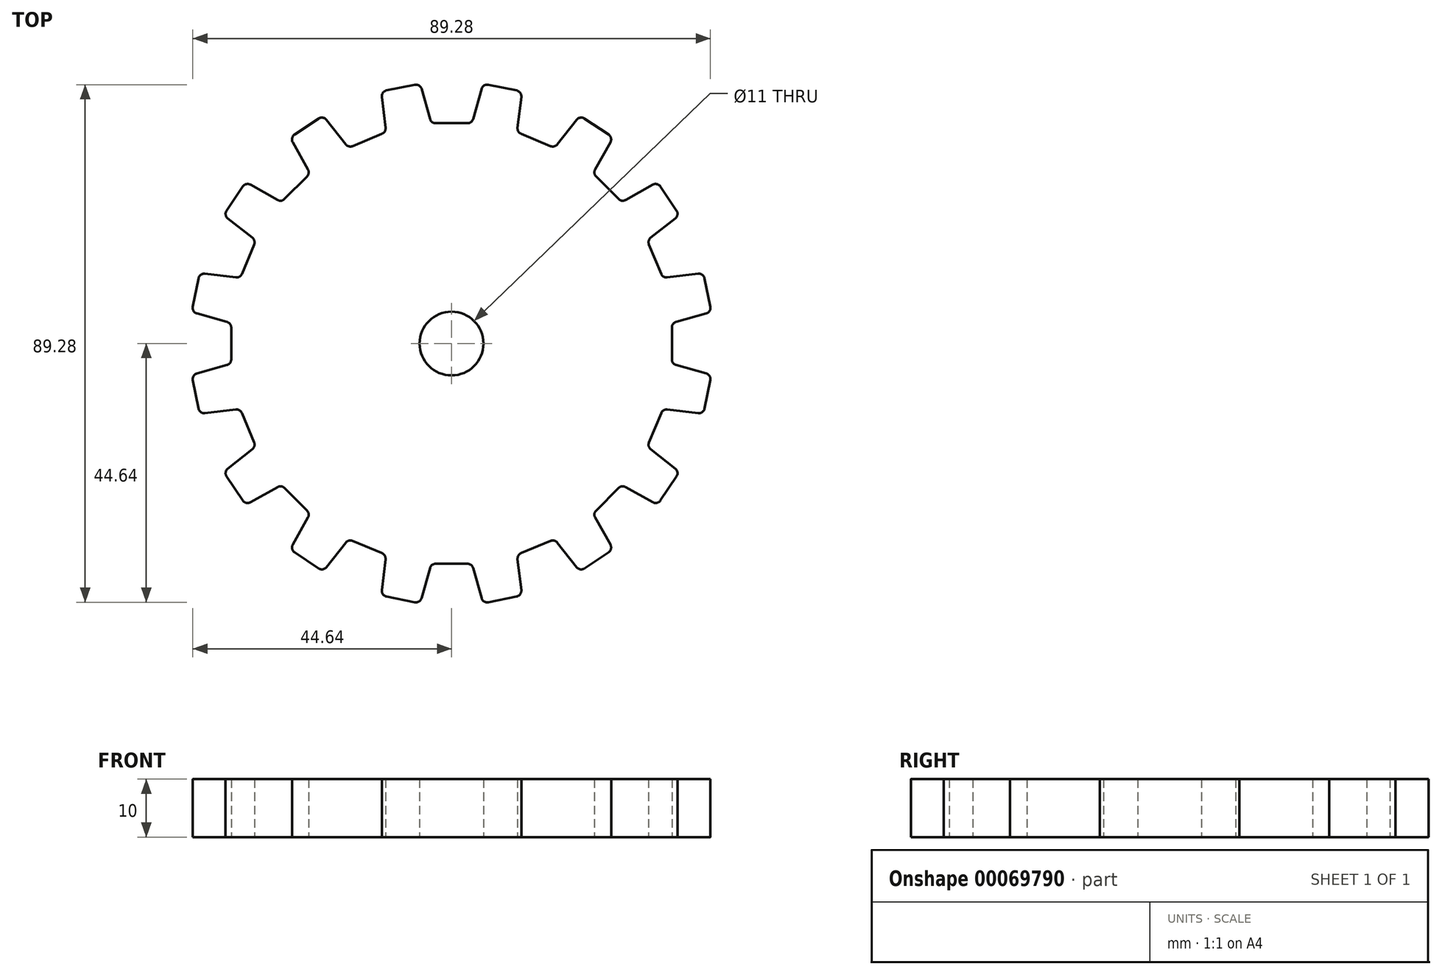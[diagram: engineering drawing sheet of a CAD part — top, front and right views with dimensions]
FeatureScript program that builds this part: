
annotation { "Feature Type Name" : "Feature", "Feature Type Description" : "" }
export const myFeature = defineFeature(function(context is Context, id is Id, definition is map)
    precondition{}
    {
        {
            var Q0;
            Q0=qCreatedBy(makeId("Top.planeOp"),FACE);
            var sketch = newSketch(context, id + "F0", { "sketchPlane" : qUnion([Q0])});
            skLineSegment(sketch, "E0", {"start": v(0, 0) * mm, "end": v(0, 50) * mm});
            skSolve(sketch);
        }
        {
            var Q0;
            Q0=qCreatedBy(makeId("Top.planeOp"),FACE);
            var sketch = newSketch(context, id + "F1", { "sketchPlane" : qUnion([Q0])});
            skLineSegment(sketch, "E1", {"start": v(0, 38) * mm, "end": v(2.75, 38) * mm});
            skLineSegment(sketch, "E2", {"start": v(3.71, 38.73) * mm, "end": v(5.17, 43.91) * mm});
            skLineSegment(sketch, "E3", {"start": v(6.33, 44.62) * mm, "end": v(8.78, 44.14) * mm});
            skPoint(sketch, "E4.visualSharp", {"position": v(5.42, 44.8) * mm});
            skArc(sketch, "E4.filletArc", {"start": v(6.33, 44.62) * mm, "mid": v(5.6, 44.5) * mm, "end": v(5.17, 43.91) * mm});
            skPoint(sketch, "E5.visualSharp", {"position": v(3.5, 38) * mm});
            skArc(sketch, "E5.filletArc", {"start": v(2.75, 38) * mm, "mid": v(3.35, 38.2) * mm, "end": v(3.71, 38.73) * mm});
            skLineSegment(sketch, "E6.MirrorCS", {"start": v(-6.33, 44.62) * mm, "end": v(-8.78, 44.14) * mm});
            skArc(sketch, "E7.MirrorCS", {"start": v(-6.33, 44.62) * mm, "mid": v(-5.6, 44.5) * mm, "end": v(-5.17, 43.91) * mm});
            skLineSegment(sketch, "E8.MirrorCS", {"start": v(0, 38) * mm, "end": v(-2.75, 38) * mm});
            skLineSegment(sketch, "E9.MirrorCS", {"start": v(-3.71, 38.73) * mm, "end": v(-5.17, 43.91) * mm});
            skArc(sketch, "E10.MirrorCS", {"start": v(-2.75, 38) * mm, "mid": v(-3.35, 38.2) * mm, "end": v(-3.71, 38.73) * mm});
            skLineSegment(sketch, "E11.1.0", {"start": v(-22.92, 38.8) * mm, "end": v(-25, 37.42) * mm});
            skArc(sketch, "E11.1.1", {"start": v(-22.92, 38.8) * mm, "mid": v(-22.2, 38.96) * mm, "end": v(-21.58, 38.6) * mm});
            skLineSegment(sketch, "E11.1.2", {"start": v(-18.25, 34.36) * mm, "end": v(-21.58, 38.6) * mm});
            skArc(sketch, "E11.1.3", {"start": v(-17.08, 34.06) * mm, "mid": v(-17.72, 34.01) * mm, "end": v(-18.25, 34.36) * mm});
            skLineSegment(sketch, "E11.1.4", {"start": v(-14.54, 35.1) * mm, "end": v(-17.08, 34.06) * mm});
            skLineSegment(sketch, "E11.1.5", {"start": v(-14.54, 35.1) * mm, "end": v(-12, 36.16) * mm});
            skArc(sketch, "E11.1.6", {"start": v(-12, 36.16) * mm, "mid": v(-11.52, 36.58) * mm, "end": v(-11.4, 37.2) * mm});
            skLineSegment(sketch, "E11.1.7", {"start": v(-11.4, 37.2) * mm, "end": v(-12.03, 42.55) * mm});
            skArc(sketch, "E11.1.8", {"start": v(-11.23, 43.65) * mm, "mid": v(-11.85, 43.25) * mm, "end": v(-12.03, 42.55) * mm});
            skLineSegment(sketch, "E11.1.9", {"start": v(-11.23, 43.65) * mm, "end": v(-8.78, 44.14) * mm});
            skLineSegment(sketch, "E11.2.0", {"start": v(-36.03, 27.08) * mm, "end": v(-37.42, 25) * mm});
            skArc(sketch, "E11.2.1", {"start": v(-36.03, 27.08) * mm, "mid": v(-35.43, 27.5) * mm, "end": v(-34.7, 27.4) * mm});
            skLineSegment(sketch, "E11.2.2", {"start": v(-30.01, 24.76) * mm, "end": v(-34.7, 27.4) * mm});
            skArc(sketch, "E11.2.3", {"start": v(-28.81, 24.93) * mm, "mid": v(-29.39, 24.64) * mm, "end": v(-30.01, 24.76) * mm});
            skLineSegment(sketch, "E11.2.4", {"start": v(-26.87, 26.87) * mm, "end": v(-28.81, 24.93) * mm});
            skLineSegment(sketch, "E11.2.5", {"start": v(-26.87, 26.87) * mm, "end": v(-24.93, 28.81) * mm});
            skArc(sketch, "E11.2.6", {"start": v(-24.93, 28.81) * mm, "mid": v(-24.64, 29.39) * mm, "end": v(-24.76, 30.01) * mm});
            skLineSegment(sketch, "E11.2.7", {"start": v(-24.76, 30.01) * mm, "end": v(-27.4, 34.7) * mm});
            skArc(sketch, "E11.2.8", {"start": v(-27.08, 36.03) * mm, "mid": v(-27.5, 35.43) * mm, "end": v(-27.4, 34.7) * mm});
            skLineSegment(sketch, "E11.2.9", {"start": v(-27.08, 36.03) * mm, "end": v(-25, 37.42) * mm});
            skLineSegment(sketch, "E11.3.0", {"start": v(-43.65, 11.23) * mm, "end": v(-44.14, 8.78) * mm});
            skArc(sketch, "E11.3.1", {"start": v(-43.65, 11.23) * mm, "mid": v(-43.25, 11.85) * mm, "end": v(-42.55, 12.03) * mm});
            skLineSegment(sketch, "E11.3.2", {"start": v(-37.2, 11.4) * mm, "end": v(-42.55, 12.03) * mm});
            skArc(sketch, "E11.3.3", {"start": v(-36.16, 12) * mm, "mid": v(-36.58, 11.52) * mm, "end": v(-37.2, 11.4) * mm});
            skLineSegment(sketch, "E11.3.4", {"start": v(-35.1, 14.54) * mm, "end": v(-36.16, 12) * mm});
            skLineSegment(sketch, "E11.3.5", {"start": v(-35.1, 14.54) * mm, "end": v(-34.06, 17.08) * mm});
            skArc(sketch, "E11.3.6", {"start": v(-34.06, 17.08) * mm, "mid": v(-34.01, 17.72) * mm, "end": v(-34.36, 18.25) * mm});
            skLineSegment(sketch, "E11.3.7", {"start": v(-34.36, 18.25) * mm, "end": v(-38.6, 21.58) * mm});
            skArc(sketch, "E11.3.8", {"start": v(-38.8, 22.92) * mm, "mid": v(-38.96, 22.2) * mm, "end": v(-38.6, 21.58) * mm});
            skLineSegment(sketch, "E11.3.9", {"start": v(-38.8, 22.92) * mm, "end": v(-37.42, 25) * mm});
            skLineSegment(sketch, "E11.4.0", {"start": v(-44.62, -6.33) * mm, "end": v(-44.14, -8.78) * mm});
            skArc(sketch, "E11.4.1", {"start": v(-44.62, -6.33) * mm, "mid": v(-44.5, -5.6) * mm, "end": v(-43.91, -5.17) * mm});
            skLineSegment(sketch, "E11.4.2", {"start": v(-38.73, -3.71) * mm, "end": v(-43.91, -5.17) * mm});
            skArc(sketch, "E11.4.3", {"start": v(-38, -2.75) * mm, "mid": v(-38.2, -3.35) * mm, "end": v(-38.73, -3.71) * mm});
            skLineSegment(sketch, "E11.4.4", {"start": v(-38, 0) * mm, "end": v(-38, -2.75) * mm});
            skLineSegment(sketch, "E11.4.5", {"start": v(-38, 0) * mm, "end": v(-38, 2.75) * mm});
            skArc(sketch, "E11.4.6", {"start": v(-38, 2.75) * mm, "mid": v(-38.2, 3.35) * mm, "end": v(-38.73, 3.71) * mm});
            skLineSegment(sketch, "E11.4.7", {"start": v(-38.73, 3.71) * mm, "end": v(-43.91, 5.17) * mm});
            skArc(sketch, "E11.4.8", {"start": v(-44.62, 6.33) * mm, "mid": v(-44.5, 5.6) * mm, "end": v(-43.91, 5.17) * mm});
            skLineSegment(sketch, "E11.4.9", {"start": v(-44.62, 6.33) * mm, "end": v(-44.14, 8.78) * mm});
            skLineSegment(sketch, "E11.5.0", {"start": v(-38.8, -22.92) * mm, "end": v(-37.42, -25) * mm});
            skArc(sketch, "E11.5.1", {"start": v(-38.8, -22.92) * mm, "mid": v(-38.96, -22.2) * mm, "end": v(-38.6, -21.58) * mm});
            skLineSegment(sketch, "E11.5.2", {"start": v(-34.36, -18.25) * mm, "end": v(-38.6, -21.58) * mm});
            skArc(sketch, "E11.5.3", {"start": v(-34.06, -17.08) * mm, "mid": v(-34.01, -17.72) * mm, "end": v(-34.36, -18.25) * mm});
            skLineSegment(sketch, "E11.5.4", {"start": v(-35.1, -14.54) * mm, "end": v(-34.06, -17.08) * mm});
            skLineSegment(sketch, "E11.5.5", {"start": v(-35.1, -14.54) * mm, "end": v(-36.16, -12) * mm});
            skArc(sketch, "E11.5.6", {"start": v(-36.16, -12) * mm, "mid": v(-36.58, -11.52) * mm, "end": v(-37.2, -11.4) * mm});
            skLineSegment(sketch, "E11.5.7", {"start": v(-37.2, -11.4) * mm, "end": v(-42.55, -12.03) * mm});
            skArc(sketch, "E11.5.8", {"start": v(-43.65, -11.23) * mm, "mid": v(-43.25, -11.85) * mm, "end": v(-42.55, -12.03) * mm});
            skLineSegment(sketch, "E11.5.9", {"start": v(-43.65, -11.23) * mm, "end": v(-44.14, -8.78) * mm});
            skLineSegment(sketch, "E11.6.0", {"start": v(-27.08, -36.03) * mm, "end": v(-25, -37.42) * mm});
            skArc(sketch, "E11.6.1", {"start": v(-27.08, -36.03) * mm, "mid": v(-27.5, -35.43) * mm, "end": v(-27.4, -34.7) * mm});
            skLineSegment(sketch, "E11.6.2", {"start": v(-24.76, -30.01) * mm, "end": v(-27.4, -34.7) * mm});
            skArc(sketch, "E11.6.3", {"start": v(-24.93, -28.81) * mm, "mid": v(-24.64, -29.39) * mm, "end": v(-24.76, -30.01) * mm});
            skLineSegment(sketch, "E11.6.4", {"start": v(-26.87, -26.87) * mm, "end": v(-24.93, -28.81) * mm});
            skLineSegment(sketch, "E11.6.5", {"start": v(-26.87, -26.87) * mm, "end": v(-28.81, -24.93) * mm});
            skArc(sketch, "E11.6.6", {"start": v(-28.81, -24.93) * mm, "mid": v(-29.39, -24.64) * mm, "end": v(-30.01, -24.76) * mm});
            skLineSegment(sketch, "E11.6.7", {"start": v(-30.01, -24.76) * mm, "end": v(-34.7, -27.4) * mm});
            skArc(sketch, "E11.6.8", {"start": v(-36.03, -27.08) * mm, "mid": v(-35.43, -27.5) * mm, "end": v(-34.7, -27.4) * mm});
            skLineSegment(sketch, "E11.6.9", {"start": v(-36.03, -27.08) * mm, "end": v(-37.42, -25) * mm});
            skLineSegment(sketch, "E11.7.0", {"start": v(-11.23, -43.65) * mm, "end": v(-8.78, -44.14) * mm});
            skArc(sketch, "E11.7.1", {"start": v(-11.23, -43.65) * mm, "mid": v(-11.85, -43.25) * mm, "end": v(-12.03, -42.55) * mm});
            skLineSegment(sketch, "E11.7.2", {"start": v(-11.4, -37.2) * mm, "end": v(-12.03, -42.55) * mm});
            skArc(sketch, "E11.7.3", {"start": v(-12, -36.16) * mm, "mid": v(-11.52, -36.58) * mm, "end": v(-11.4, -37.2) * mm});
            skLineSegment(sketch, "E11.7.4", {"start": v(-14.54, -35.1) * mm, "end": v(-12, -36.16) * mm});
            skLineSegment(sketch, "E11.7.5", {"start": v(-14.54, -35.1) * mm, "end": v(-17.08, -34.06) * mm});
            skArc(sketch, "E11.7.6", {"start": v(-17.08, -34.06) * mm, "mid": v(-17.72, -34.01) * mm, "end": v(-18.25, -34.36) * mm});
            skLineSegment(sketch, "E11.7.7", {"start": v(-18.25, -34.36) * mm, "end": v(-21.58, -38.6) * mm});
            skArc(sketch, "E11.7.8", {"start": v(-22.92, -38.8) * mm, "mid": v(-22.2, -38.96) * mm, "end": v(-21.58, -38.6) * mm});
            skLineSegment(sketch, "E11.7.9", {"start": v(-22.92, -38.8) * mm, "end": v(-25, -37.42) * mm});
            skLineSegment(sketch, "E11.8.0", {"start": v(6.33, -44.62) * mm, "end": v(8.78, -44.14) * mm});
            skArc(sketch, "E11.8.1", {"start": v(6.33, -44.62) * mm, "mid": v(5.6, -44.5) * mm, "end": v(5.17, -43.91) * mm});
            skLineSegment(sketch, "E11.8.2", {"start": v(3.71, -38.73) * mm, "end": v(5.17, -43.91) * mm});
            skArc(sketch, "E11.8.3", {"start": v(2.75, -38) * mm, "mid": v(3.35, -38.2) * mm, "end": v(3.71, -38.73) * mm});
            skLineSegment(sketch, "E11.8.4", {"start": v(0, -38) * mm, "end": v(2.75, -38) * mm});
            skLineSegment(sketch, "E11.8.5", {"start": v(0, -38) * mm, "end": v(-2.75, -38) * mm});
            skArc(sketch, "E11.8.6", {"start": v(-2.75, -38) * mm, "mid": v(-3.35, -38.2) * mm, "end": v(-3.71, -38.73) * mm});
            skLineSegment(sketch, "E11.8.7", {"start": v(-3.71, -38.73) * mm, "end": v(-5.17, -43.91) * mm});
            skArc(sketch, "E11.8.8", {"start": v(-6.33, -44.62) * mm, "mid": v(-5.6, -44.5) * mm, "end": v(-5.17, -43.91) * mm});
            skLineSegment(sketch, "E11.8.9", {"start": v(-6.33, -44.62) * mm, "end": v(-8.78, -44.14) * mm});
            skLineSegment(sketch, "E11.9.0", {"start": v(22.92, -38.8) * mm, "end": v(25, -37.42) * mm});
            skArc(sketch, "E11.9.1", {"start": v(22.92, -38.8) * mm, "mid": v(22.2, -38.96) * mm, "end": v(21.58, -38.6) * mm});
            skLineSegment(sketch, "E11.9.2", {"start": v(18.25, -34.36) * mm, "end": v(21.58, -38.6) * mm});
            skArc(sketch, "E11.9.3", {"start": v(17.08, -34.06) * mm, "mid": v(17.72, -34.01) * mm, "end": v(18.25, -34.36) * mm});
            skLineSegment(sketch, "E11.9.4", {"start": v(14.54, -35.1) * mm, "end": v(17.08, -34.06) * mm});
            skLineSegment(sketch, "E11.9.5", {"start": v(14.54, -35.1) * mm, "end": v(12, -36.16) * mm});
            skArc(sketch, "E11.9.6", {"start": v(12, -36.16) * mm, "mid": v(11.52, -36.58) * mm, "end": v(11.4, -37.2) * mm});
            skLineSegment(sketch, "E11.9.7", {"start": v(11.4, -37.2) * mm, "end": v(12.03, -42.55) * mm});
            skArc(sketch, "E11.9.8", {"start": v(11.23, -43.65) * mm, "mid": v(11.85, -43.25) * mm, "end": v(12.03, -42.55) * mm});
            skLineSegment(sketch, "E11.9.9", {"start": v(11.23, -43.65) * mm, "end": v(8.78, -44.14) * mm});
            skLineSegment(sketch, "E11.10.0", {"start": v(36.03, -27.08) * mm, "end": v(37.42, -25) * mm});
            skArc(sketch, "E11.10.1", {"start": v(36.03, -27.08) * mm, "mid": v(35.43, -27.5) * mm, "end": v(34.7, -27.4) * mm});
            skLineSegment(sketch, "E11.10.2", {"start": v(30.01, -24.76) * mm, "end": v(34.7, -27.4) * mm});
            skArc(sketch, "E11.10.3", {"start": v(28.81, -24.93) * mm, "mid": v(29.39, -24.64) * mm, "end": v(30.01, -24.76) * mm});
            skLineSegment(sketch, "E11.10.4", {"start": v(26.87, -26.87) * mm, "end": v(28.81, -24.93) * mm});
            skLineSegment(sketch, "E11.10.5", {"start": v(26.87, -26.87) * mm, "end": v(24.93, -28.81) * mm});
            skArc(sketch, "E11.10.6", {"start": v(24.93, -28.81) * mm, "mid": v(24.64, -29.39) * mm, "end": v(24.76, -30.01) * mm});
            skLineSegment(sketch, "E11.10.7", {"start": v(24.76, -30.01) * mm, "end": v(27.4, -34.7) * mm});
            skArc(sketch, "E11.10.8", {"start": v(27.08, -36.03) * mm, "mid": v(27.5, -35.43) * mm, "end": v(27.4, -34.7) * mm});
            skLineSegment(sketch, "E11.10.9", {"start": v(27.08, -36.03) * mm, "end": v(25, -37.42) * mm});
            skLineSegment(sketch, "E11.11.0", {"start": v(43.65, -11.23) * mm, "end": v(44.14, -8.78) * mm});
            skArc(sketch, "E11.11.1", {"start": v(43.65, -11.23) * mm, "mid": v(43.25, -11.85) * mm, "end": v(42.55, -12.03) * mm});
            skLineSegment(sketch, "E11.11.2", {"start": v(37.2, -11.4) * mm, "end": v(42.55, -12.03) * mm});
            skArc(sketch, "E11.11.3", {"start": v(36.16, -12) * mm, "mid": v(36.58, -11.52) * mm, "end": v(37.2, -11.4) * mm});
            skLineSegment(sketch, "E11.11.4", {"start": v(35.1, -14.54) * mm, "end": v(36.16, -12) * mm});
            skLineSegment(sketch, "E11.11.5", {"start": v(35.1, -14.54) * mm, "end": v(34.06, -17.08) * mm});
            skArc(sketch, "E11.11.6", {"start": v(34.06, -17.08) * mm, "mid": v(34.01, -17.72) * mm, "end": v(34.36, -18.25) * mm});
            skLineSegment(sketch, "E11.11.7", {"start": v(34.36, -18.25) * mm, "end": v(38.6, -21.58) * mm});
            skArc(sketch, "E11.11.8", {"start": v(38.8, -22.92) * mm, "mid": v(38.96, -22.2) * mm, "end": v(38.6, -21.58) * mm});
            skLineSegment(sketch, "E11.11.9", {"start": v(38.8, -22.92) * mm, "end": v(37.42, -25) * mm});
            skLineSegment(sketch, "E11.12.0", {"start": v(44.62, 6.33) * mm, "end": v(44.14, 8.78) * mm});
            skArc(sketch, "E11.12.1", {"start": v(44.62, 6.33) * mm, "mid": v(44.5, 5.6) * mm, "end": v(43.91, 5.17) * mm});
            skLineSegment(sketch, "E11.12.2", {"start": v(38.73, 3.71) * mm, "end": v(43.91, 5.17) * mm});
            skArc(sketch, "E11.12.3", {"start": v(38, 2.75) * mm, "mid": v(38.2, 3.35) * mm, "end": v(38.73, 3.71) * mm});
            skLineSegment(sketch, "E11.12.4", {"start": v(38, 0) * mm, "end": v(38, 2.75) * mm});
            skLineSegment(sketch, "E11.12.5", {"start": v(38, 0) * mm, "end": v(38, -2.75) * mm});
            skArc(sketch, "E11.12.6", {"start": v(38, -2.75) * mm, "mid": v(38.2, -3.35) * mm, "end": v(38.73, -3.71) * mm});
            skLineSegment(sketch, "E11.12.7", {"start": v(38.73, -3.71) * mm, "end": v(43.91, -5.17) * mm});
            skArc(sketch, "E11.12.8", {"start": v(44.62, -6.33) * mm, "mid": v(44.5, -5.6) * mm, "end": v(43.91, -5.17) * mm});
            skLineSegment(sketch, "E11.12.9", {"start": v(44.62, -6.33) * mm, "end": v(44.14, -8.78) * mm});
            skLineSegment(sketch, "E11.13.0", {"start": v(38.8, 22.92) * mm, "end": v(37.42, 25) * mm});
            skArc(sketch, "E11.13.1", {"start": v(38.8, 22.92) * mm, "mid": v(38.96, 22.2) * mm, "end": v(38.6, 21.58) * mm});
            skLineSegment(sketch, "E11.13.2", {"start": v(34.36, 18.25) * mm, "end": v(38.6, 21.58) * mm});
            skArc(sketch, "E11.13.3", {"start": v(34.06, 17.08) * mm, "mid": v(34.01, 17.72) * mm, "end": v(34.36, 18.25) * mm});
            skLineSegment(sketch, "E11.13.4", {"start": v(35.1, 14.54) * mm, "end": v(34.06, 17.08) * mm});
            skLineSegment(sketch, "E11.13.5", {"start": v(35.1, 14.54) * mm, "end": v(36.16, 12) * mm});
            skArc(sketch, "E11.13.6", {"start": v(36.16, 12) * mm, "mid": v(36.58, 11.52) * mm, "end": v(37.2, 11.4) * mm});
            skLineSegment(sketch, "E11.13.7", {"start": v(37.2, 11.4) * mm, "end": v(42.55, 12.03) * mm});
            skArc(sketch, "E11.13.8", {"start": v(43.65, 11.23) * mm, "mid": v(43.25, 11.85) * mm, "end": v(42.55, 12.03) * mm});
            skLineSegment(sketch, "E11.13.9", {"start": v(43.65, 11.23) * mm, "end": v(44.14, 8.78) * mm});
            skLineSegment(sketch, "E11.14.0", {"start": v(27.08, 36.03) * mm, "end": v(25, 37.42) * mm});
            skArc(sketch, "E11.14.1", {"start": v(27.08, 36.03) * mm, "mid": v(27.5, 35.43) * mm, "end": v(27.4, 34.7) * mm});
            skLineSegment(sketch, "E11.14.2", {"start": v(24.76, 30.01) * mm, "end": v(27.4, 34.7) * mm});
            skArc(sketch, "E11.14.3", {"start": v(24.93, 28.81) * mm, "mid": v(24.64, 29.39) * mm, "end": v(24.76, 30.01) * mm});
            skLineSegment(sketch, "E11.14.4", {"start": v(26.87, 26.87) * mm, "end": v(24.93, 28.81) * mm});
            skLineSegment(sketch, "E11.14.5", {"start": v(26.87, 26.87) * mm, "end": v(28.81, 24.93) * mm});
            skArc(sketch, "E11.14.6", {"start": v(28.81, 24.93) * mm, "mid": v(29.39, 24.64) * mm, "end": v(30.01, 24.76) * mm});
            skLineSegment(sketch, "E11.14.7", {"start": v(30.01, 24.76) * mm, "end": v(34.7, 27.4) * mm});
            skArc(sketch, "E11.14.8", {"start": v(36.03, 27.08) * mm, "mid": v(35.43, 27.5) * mm, "end": v(34.7, 27.4) * mm});
            skLineSegment(sketch, "E11.14.9", {"start": v(36.03, 27.08) * mm, "end": v(37.42, 25) * mm});
            skLineSegment(sketch, "E11.15.0", {"start": v(11.23, 43.65) * mm, "end": v(8.78, 44.14) * mm});
            skArc(sketch, "E11.15.1", {"start": v(11.23, 43.65) * mm, "mid": v(11.85, 43.25) * mm, "end": v(12.03, 42.55) * mm});
            skLineSegment(sketch, "E11.15.2", {"start": v(11.4, 37.2) * mm, "end": v(12.03, 42.55) * mm});
            skArc(sketch, "E11.15.3", {"start": v(12, 36.16) * mm, "mid": v(11.52, 36.58) * mm, "end": v(11.4, 37.2) * mm});
            skLineSegment(sketch, "E11.15.4", {"start": v(14.54, 35.1) * mm, "end": v(12, 36.16) * mm});
            skLineSegment(sketch, "E11.15.5", {"start": v(14.54, 35.1) * mm, "end": v(17.08, 34.06) * mm});
            skArc(sketch, "E11.15.6", {"start": v(17.08, 34.06) * mm, "mid": v(17.72, 34.01) * mm, "end": v(18.25, 34.36) * mm});
            skLineSegment(sketch, "E11.15.7", {"start": v(18.25, 34.36) * mm, "end": v(21.58, 38.6) * mm});
            skArc(sketch, "E11.15.8", {"start": v(22.92, 38.8) * mm, "mid": v(22.2, 38.96) * mm, "end": v(21.58, 38.6) * mm});
            skLineSegment(sketch, "E11.15.9", {"start": v(22.92, 38.8) * mm, "end": v(25, 37.42) * mm});
            skPoint(sketch, "E11.center", {"position": v(0, 0) * mm});
            skCircle(sketch, "E12", {"center": v(0, 0) * mm, "radius": 5.5 * mm});
            skSolve(sketch);
        }
        {
            var Q0;
            Q0 = qSketchRegion(id + "F1", true);
            extrude(context, id + "F2", {"entities" : qUnion([Q0]), "depth" : 10 * mm});
        }
    });
